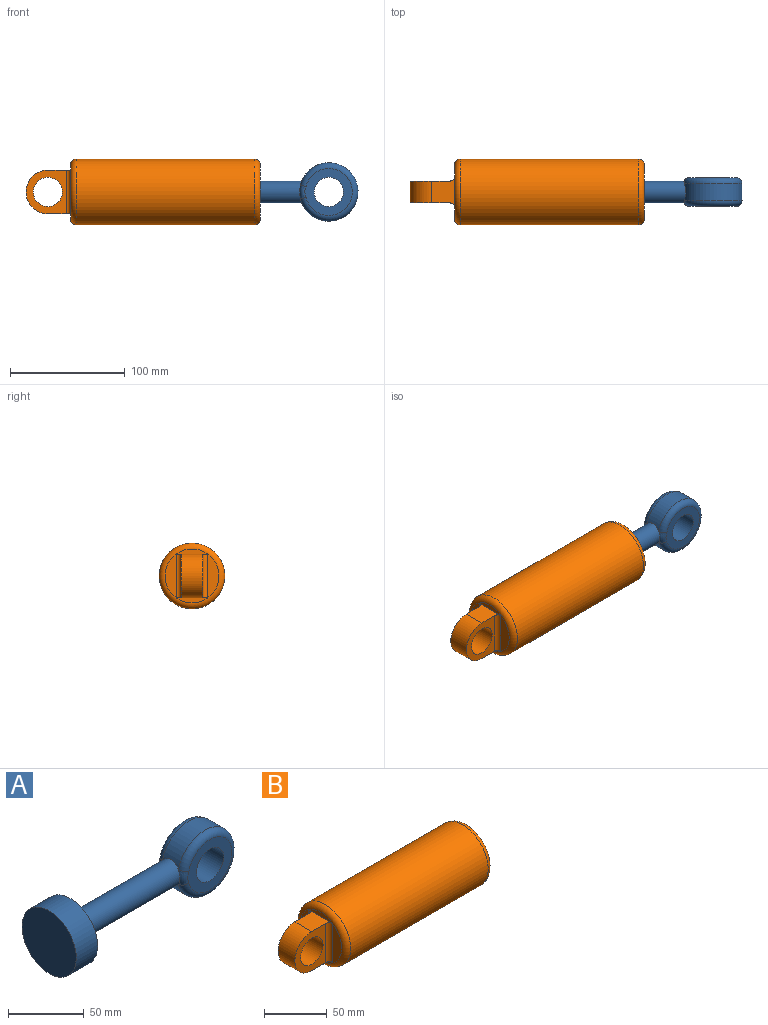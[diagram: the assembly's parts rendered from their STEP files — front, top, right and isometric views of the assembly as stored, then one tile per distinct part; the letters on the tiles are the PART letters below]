
ASSEMBLY  parts=2 mates=1
PART A: 12 faces, bbox 165.6x50.8x55 mm
  f0: cylinder r=9.53mm len=94.59mm, axis (-1,0,0), area 5616mm2, adj f3,f4,f9,f11
  f1: cylinder r=25.4mm len=50.8mm, axis (1,0,0), area 3191.9mm2, adj f2,f3
  f2: plane 50.8x50.8mm, normal (-1,0,0), area 2026.8mm2, adj f1
  f3: plane 50.8x50.8mm, normal (1,0,0), area 1741.8mm2, adj f0,f1
  f4: cylinder r=25.4mm len=50.8mm, axis (0,1,0), area 2136.2mm2, adj f0,f8,f10
  f5: cylinder r=12.7mm len=25.4mm, axis (0,1,0), area 1994.9mm2, adj f6,f7
  f6: plane 41.23x40.8mm, normal (0,-1,0), area 802.7mm2, adj f5,f10,f11
  f7: plane 41.23x40.8mm, normal (0,1,0), area 802.7mm2, adj f5,f8,f9
  f8: torus R=20.4mm, axis (0,-1,0), area 1077.4mm2, adj f4,f7,f9
  f9: bspline ~13.18x5.81mm, area 70.7mm2, adj f0,f7,f8
  f10: torus R=20.4mm, axis (0,-1,0), area 1077.4mm2, adj f4,f6,f11
  f11: bspline ~13.18x5.82mm, area 70.7mm2, adj f0,f6,f10
PART B: 17 faces, bbox 203.8x61.9x61.9 mm
  f0: cylinder r=28.57mm len=154.94mm, axis (-1,0,0), area 27818.2mm2, adj f2,f16
  f1: plane 46.99x46.99mm, normal (-1,0,0), area 718.1mm2, adj f2,f3,f4,f9,f10
  f2: torus R=23.49mm, axis (1,0,0), area 1340.1mm2, adj f0,f1
  f3: plane 26.67x19.67mm, normal (0,0,1), area 380.9mm2, adj f1,f5,f6,f7,f9,f10
  f4: plane 26.67x19.91mm, normal (0,0,-1), area 385.5mm2, adj f1,f5,f6,f7,f9,f10
  f5: plane 38.1x34.91mm, normal (0,-1,0), area 667.5mm2, adj f3,f4,f7,f8,f9
  f6: plane 38.1x34.91mm, normal (0,1,0), area 667.5mm2, adj f3,f4,f7,f8,f10
  f7: cylinder r=19.05mm len=38.1mm, axis (0,1,0), area 1135.5mm2, adj f3,f4,f5,f6
  f8: cylinder r=12.7mm len=25.4mm, axis (0,1,0), area 1520.1mm2, adj f5,f6
  f9: cylinder r=3.81mm len=38.1mm, axis (0,0,-1), area 228mm2, adj f1,f3,f4,f5
  f10: cylinder r=3.81mm len=38.1mm, axis (0,0,1), area 228mm2, adj f1,f3,f4,f6
  f11: plane 50.8x50.8mm, normal (-1,0,0), area 1741.8mm2, adj f12,f15
  f12: cylinder r=9.53mm len=19.05mm, axis (-1,0,0), area 380mm2, adj f11,f13
  f13: plane 46.99x46.99mm, normal (1,0,0), area 1449.2mm2, adj f12,f16
  f14: plane 50.8x50.8mm, normal (1,0,0), area 2026.8mm2, adj f15
  f15: cylinder r=25.4mm len=152.4mm, axis (-1,0,0), area 24322mm2, adj f11,f14
  f16: torus R=23.49mm, axis (1,0,0), area 1340.1mm2, adj f0,f13
PLACE A rot(axis=(0.07,0.1,0.99),0deg) t=(101.72,84.13,-35.07)mm
PLACE B t=(1.5,84.13,-35.07)mm
MATE slider B.f0 <-> A.f0  axis (-1,0,0) through (155.17,84.13,-35.07)mm
